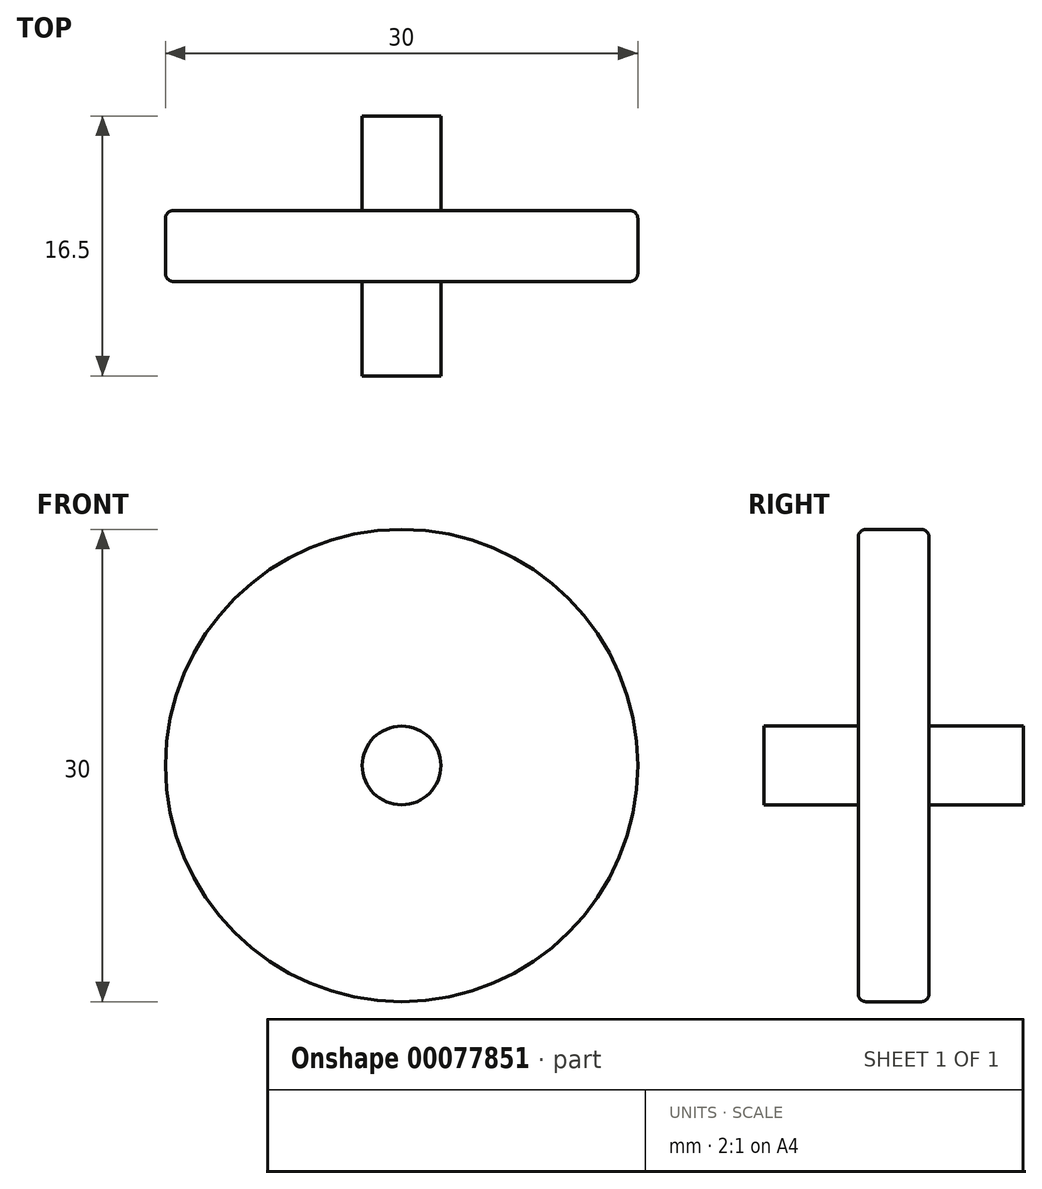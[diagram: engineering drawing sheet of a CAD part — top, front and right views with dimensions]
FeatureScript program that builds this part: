
annotation { "Feature Type Name" : "Feature", "Feature Type Description" : "" }
export const myFeature = defineFeature(function(context is Context, id is Id, definition is map)
    precondition{}
    {
        {
            var Q0;
            Q0=qCreatedBy(makeId("Front.planeOp"),FACE);
            var sketch = newSketch(context, id + "F0", { "sketchPlane" : qUnion([Q0])});
            skCircle(sketch, "E0", {"center": v(0, 0) * mm, "radius": 15 * mm});
            skCircle(sketch, "E1", {"center": v(0, 0) * mm, "radius": 2.5 * mm});
            skSolve(sketch);
        }
        {
            var Q0;
            Q0=makeQuery(id+"F0.imprint","IMPRINT",FACE,{"disambiguationData":[TD([[makeQuery(id+"F0.imprint","IMPRINT",EDGE,{"derivedFrom":sQuery(id+"F0.wireOp",EDGE,"E0")}),1.0]])]});
            extrude(context, id + "F1", {"entities" : qUnion([Q0]), "endBound" : BoundingType.SYMMETRIC, "depth" : 4.5 * mm});
        }
        {
            var Q0;
            Q0=makeQuery(id+"F0.imprint","IMPRINT",FACE,{"disambiguationData":[TD([[makeQuery(id+"F0.imprint","IMPRINT",EDGE,{"derivedFrom":sQuery(id+"F0.wireOp",EDGE,"E1")}),1.0]])]});
            extrude(context, id + "F2", {"entities" : qUnion([Q0]), "operationType" : NewBodyOperationType.ADD, "endBound" : BoundingType.SYMMETRIC, "depth" : 16.5 * mm});
        }
        {
            var Q0;
            Q0=makeQuery(id+"F1.opExtrude","CAP_EDGE",EDGE,{"disambiguationData":[OSD([sQuery(id+"F0.wireOp",EDGE,"E0")])],"isStart":false});
            var Q1;
            Q1=makeQuery(id+"F1.opExtrude","CAP_EDGE",EDGE,{"disambiguationData":[OSD([sQuery(id+"F0.wireOp",EDGE,"E0")])],"isStart":true});
            fillet(context, id + "F3", {"entities" : qUnion([Q0, Q1]), "radius" : 0.5 * mm, "tangentPropagation" : true, "allowEdgeOverflow" : false});
        }
    });
